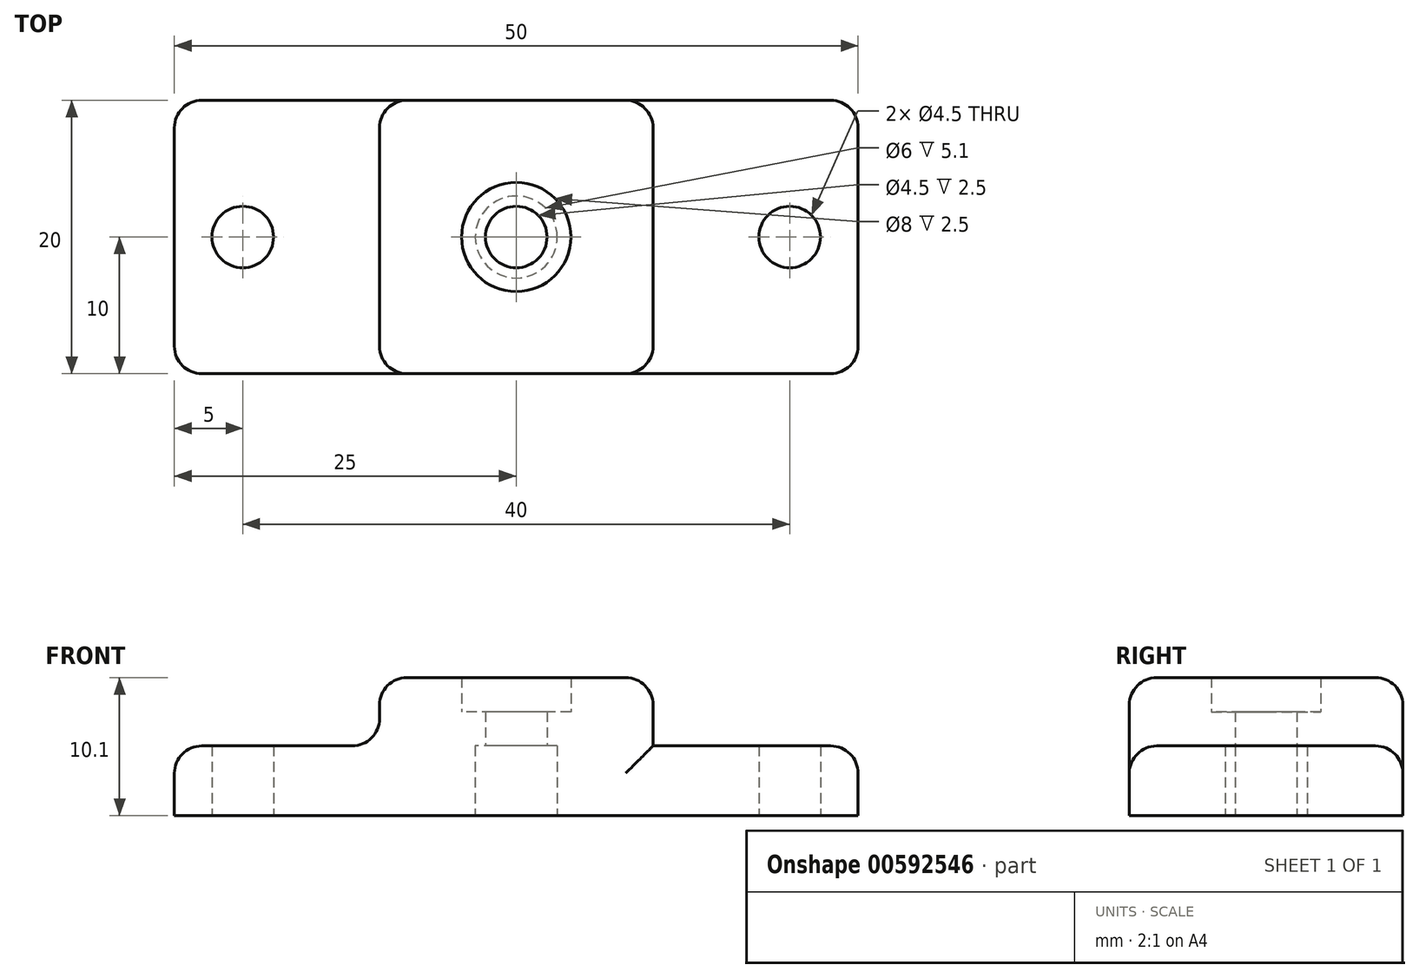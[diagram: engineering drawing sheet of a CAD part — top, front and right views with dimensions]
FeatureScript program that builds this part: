
annotation { "Feature Type Name" : "Feature", "Feature Type Description" : "" }
export const myFeature = defineFeature(function(context is Context, id is Id, definition is map)
    precondition{}
    {
        {
            var Q0;
            Q0=qCreatedBy(makeId("Top.planeOp"),FACE);
            var sketch = newSketch(context, id + "F0", { "sketchPlane" : qUnion([Q0])});
            skLineSegment(sketch, "E0.bottom", {"start": v(-25, 10) * mm, "end": v(25, 10) * mm});
            skLineSegment(sketch, "E0.top", {"start": v(-25, -10) * mm, "end": v(25, -10) * mm});
            skLineSegment(sketch, "E0.left", {"start": v(-25, 10) * mm, "end": v(-25, -10) * mm});
            skLineSegment(sketch, "E0.right", {"start": v(25, 10) * mm, "end": v(25, -10) * mm});
            skPoint(sketch, "E0.middle", {"position": v(0, 0) * mm});
            skCircle(sketch, "E1", {"center": v(0, 0) * mm, "radius": 3 * mm});
            skCircle(sketch, "E2", {"center": v(0, 0) * mm, "radius": 2.25 * mm});
            skCircle(sketch, "E3", {"center": v(0, 0) * mm, "radius": 4 * mm});
            skCircle(sketch, "E4", {"center": v(-20, 0) * mm, "radius": 2.25 * mm});
            skCircle(sketch, "E5", {"center": v(20, 0) * mm, "radius": 2.25 * mm});
            skSolve(sketch);
        }
        {
            var Q0;
            Q0=makeQuery(id+"F0.imprint","IMPRINT",FACE,{"disambiguationData":[TD([[makeQuery(id+"F0.imprint","IMPRINT",EDGE,{"derivedFrom":sQuery(id+"F0.wireOp",EDGE,"E0.bottom")}),-1.0]])]});
            var Q1;
            Q1=makeQuery(id+"F0.imprint","IMPRINT",FACE,{"disambiguationData":[TD([[makeQuery(id+"F0.imprint","IMPRINT",EDGE,{"derivedFrom":sQuery(id+"F0.wireOp",EDGE,"E1")}),-1.0]])]});
            extrude(context, id + "F1", {"entities" : qUnion([Q0, Q1]), "depth" : 5.1 * mm, "offsetDistance" : 25 * mm});
        }
        {
            var Q0;
            Q0=makeQuery(id+"F1.opExtrude","CAP_FACE",FACE,{"disambiguationData":[OSD([sQuery(id+"F0.wireOp",EDGE,"E0.bottom"),sQuery(id+"F0.wireOp",EDGE,"E0.top"),sQuery(id+"F0.wireOp",EDGE,"E0.left"),sQuery(id+"F0.wireOp",EDGE,"E0.right"),sQuery(id+"F0.wireOp",EDGE,"E1"),sQuery(id+"F0.wireOp",EDGE,"E4"),sQuery(id+"F0.wireOp",EDGE,"E5")])],"isStart":false});
            var sketch = newSketch(context, id + "F2", { "sketchPlane" : qUnion([Q0])});
            skLineSegment(sketch, "E6.bottom", {"start": v(10, -10) * mm, "end": v(-10, -10) * mm});
            skLineSegment(sketch, "E6.top", {"start": v(10, 10) * mm, "end": v(-10, 10) * mm});
            skLineSegment(sketch, "E6.left", {"start": v(10, -10) * mm, "end": v(10, 10) * mm});
            skLineSegment(sketch, "E6.right", {"start": v(-10, -10) * mm, "end": v(-10, 10) * mm});
            skPoint(sketch, "E6.middle", {"position": v(0, 0) * mm});
            skCircle(sketch, "E7.0", {"center": v(0, 0) * mm, "radius": 2.25 * mm});
            skSolve(sketch);
        }
        {
            var Q0;
            Q0=makeQuery(id+"F2.imprint","IMPRINT",FACE,{"disambiguationData":[TD([[makeQuery(id+"F2.imprint","IMPRINT",EDGE,{"derivedFrom":sQuery(id+"F2.wireOp",EDGE,"E6.bottom")}),1.0]])]});
            var Q1;
            Q1=makeQuery(id+"F2.imprint","IMPRINT",FACE,{"disambiguationData":[TD([[makeQuery(id+"F2.imprint","IMPRINT",EDGE,{"derivedFrom":sQuery(id+"F2.wireOp",EDGE,"E7.0")}),-1.0]])]});
            extrude(context, id + "F3", {"entities" : qUnion([Q0, Q1]), "operationType" : NewBodyOperationType.ADD, "depth" : 2.5 * mm, "offsetDistance" : 25 * mm});
        }
        {
            var Q0;
            Q0=makeQuery(id+"F3.opExtrude","CAP_FACE",FACE,{"disambiguationData":[OSD([sQuery(id+"F2.wireOp",EDGE,"E6.bottom"),sQuery(id+"F2.wireOp",EDGE,"E6.top"),sQuery(id+"F2.wireOp",EDGE,"E6.left"),sQuery(id+"F2.wireOp",EDGE,"E6.right"),sQuery(id+"F2.wireOp",EDGE,"E7.0")])],"isStart":false});
            var sketch = newSketch(context, id + "F4", { "sketchPlane" : qUnion([Q0])});
            skCircle(sketch, "E8.0", {"center": v(0, 0) * mm, "radius": 4 * mm});
            skSolve(sketch);
        }
        {
            var Q0;
            Q0=makeQuery(id+"F4.imprint","IMPRINT",FACE,{"disambiguationData":[TD([[makeQuery(id+"F4.imprint","IMPRINT",EDGE,{"derivedFrom":sQuery(id+"F4.wireOp",EDGE,"E8.0")}),-1.0]])]});
            extrude(context, id + "F5", {"entities" : qUnion([Q0]), "operationType" : NewBodyOperationType.ADD, "depth" : 2.5 * mm, "offsetDistance" : 25 * mm});
        }
        {
            var Q0;
            Q0=makeQuery(id+"F1.opExtrude","SWEPT_EDGE",EDGE,{"disambiguationData":[OSD([sQuery(id+"F0.wireOp",EDGE,"E0.top"),sQuery(id+"F0.wireOp",EDGE,"E0.left")])]});
            var Q1;
            Q1=makeQuery(id+"F1.opExtrude","SWEPT_EDGE",EDGE,{"disambiguationData":[OSD([sQuery(id+"F0.wireOp",EDGE,"E0.top"),sQuery(id+"F0.wireOp",EDGE,"E0.right")])]});
            var Q2;
            Q2=makeQuery(id+"F1.opExtrude","SWEPT_EDGE",EDGE,{"disambiguationData":[OSD([sQuery(id+"F0.wireOp",EDGE,"E0.bottom"),sQuery(id+"F0.wireOp",EDGE,"E0.right")])]});
            var Q3;
            Q3=makeQuery(id+"F1.opExtrude","CAP_EDGE",EDGE,{"disambiguationData":[OSD([sQuery(id+"F0.wireOp",EDGE,"E0.right")])],"isStart":false});
            var Q4;
            {var subQ0=sQuery(id+"F0.wireOp",EDGE,"E0.right");var subQ1=sQuery(id+"F0.wireOp",EDGE,"E0.top");Q4=makeQuery(id+"F3.boolean.opBoolean","SPLIT",EDGE,{"disambiguationData":[TD([makeQuery(id+"F1.opExtrude","SWEPT_FACE",FACE,{"disambiguationData":[OSD([subQ0])]})])],"derivedFrom":makeQuery(id+"F1.opExtrude","CAP_EDGE",EDGE,{"disambiguationData":[OSD([subQ1])],"isStart":false})});}
            var Q5;
            {var subQ0=sQuery(id+"F0.wireOp",EDGE,"E0.right");var subQ1=sQuery(id+"F0.wireOp",EDGE,"E0.bottom");Q5=makeQuery(id+"F3.boolean.opBoolean","SPLIT",EDGE,{"disambiguationData":[TD([makeQuery(id+"F1.opExtrude","SWEPT_FACE",FACE,{"disambiguationData":[OSD([subQ0])]})])],"derivedFrom":makeQuery(id+"F1.opExtrude","CAP_EDGE",EDGE,{"disambiguationData":[OSD([subQ1])],"isStart":false})});}
            var Q6;
            {var subQ0=sQuery(id+"F0.wireOp",EDGE,"E0.left");var subQ1=sQuery(id+"F0.wireOp",EDGE,"E0.top");Q6=makeQuery(id+"F3.boolean.opBoolean","SPLIT",EDGE,{"disambiguationData":[TD([makeQuery(id+"F1.opExtrude","SWEPT_FACE",FACE,{"disambiguationData":[OSD([subQ0])]})])],"derivedFrom":makeQuery(id+"F1.opExtrude","CAP_EDGE",EDGE,{"disambiguationData":[OSD([subQ1])],"isStart":false})});}
            var Q7;
            Q7=makeQuery(id+"F1.opExtrude","CAP_EDGE",EDGE,{"disambiguationData":[OSD([sQuery(id+"F0.wireOp",EDGE,"E0.left")])],"isStart":false});
            var Q8;
            {var subQ0=sQuery(id+"F0.wireOp",EDGE,"E0.left");var subQ1=sQuery(id+"F0.wireOp",EDGE,"E0.bottom");Q8=makeQuery(id+"F3.boolean.opBoolean","SPLIT",EDGE,{"disambiguationData":[TD([makeQuery(id+"F1.opExtrude","SWEPT_FACE",FACE,{"disambiguationData":[OSD([subQ0])]})])],"derivedFrom":makeQuery(id+"F1.opExtrude","CAP_EDGE",EDGE,{"disambiguationData":[OSD([subQ1])],"isStart":false})});}
            var Q9;
            Q9=makeQuery(id+"F1.opExtrude","SWEPT_EDGE",EDGE,{"disambiguationData":[OSD([sQuery(id+"F0.wireOp",EDGE,"E0.bottom"),sQuery(id+"F0.wireOp",EDGE,"E0.left")])]});
            var Q10;
            {var subQ0=sQuery(id+"Fktommp5rpzYMpY_1.wireOp",EDGE,"151076d3-d12a-400f-b86c-be84b4d02cd2.3");var subQ1=sQuery(id+"Fktommp5rpzYMpY_1.wireOp",EDGE,"151076d3-d12a-400f-b86c-be84b4d02cd2.1");Q10=makeQuery(id+"F5.boolean.opBoolean","MERGE",EDGE,{"derivedFrom":[makeQuery(id+"FSvqePnx5guRIMX_1.boolean.opBoolean","MERGE",EDGE,{"derivedFrom":[makeQuery(id+"F3.opExtrude","SWEPT_EDGE",EDGE,{"disambiguationData":[OSD([sQuery(id+"F0.wireOp",EDGE,"E0.top"),sQuery(id+"F2.wireOp",EDGE,"E6.bottom"),sQuery(id+"F2.wireOp",EDGE,"E6.left")])]}),makeQuery(id+"FSvqePnx5guRIMX_1.opExtrude","SWEPT_EDGE",EDGE,{"disambiguationData":[OSD([subQ1,subQ0])]})]}),makeQuery(id+"F5.opExtrude","SWEPT_EDGE",EDGE,{"disambiguationData":[OSD([subQ1,subQ0])]})]});}
            var Q11;
            {var subQ0=sQuery(id+"Fktommp5rpzYMpY_1.wireOp",EDGE,"151076d3-d12a-400f-b86c-be84b4d02cd2.2");var subQ1=sQuery(id+"Fktommp5rpzYMpY_1.wireOp",EDGE,"151076d3-d12a-400f-b86c-be84b4d02cd2.1");Q11=makeQuery(id+"F5.boolean.opBoolean","MERGE",EDGE,{"derivedFrom":[makeQuery(id+"FSvqePnx5guRIMX_1.boolean.opBoolean","MERGE",EDGE,{"derivedFrom":[makeQuery(id+"F3.opExtrude","SWEPT_EDGE",EDGE,{"disambiguationData":[OSD([sQuery(id+"F0.wireOp",EDGE,"E0.bottom"),sQuery(id+"F2.wireOp",EDGE,"E6.top"),sQuery(id+"F2.wireOp",EDGE,"E6.left")])]}),makeQuery(id+"FSvqePnx5guRIMX_1.opExtrude","SWEPT_EDGE",EDGE,{"disambiguationData":[OSD([subQ1,subQ0])]})]}),makeQuery(id+"F5.opExtrude","SWEPT_EDGE",EDGE,{"disambiguationData":[OSD([subQ1,subQ0])]})]});}
            var Q12;
            {var subQ0=sQuery(id+"Fktommp5rpzYMpY_1.wireOp",EDGE,"151076d3-d12a-400f-b86c-be84b4d02cd2.3");var subQ1=sQuery(id+"Fktommp5rpzYMpY_1.wireOp",EDGE,"151076d3-d12a-400f-b86c-be84b4d02cd2.0");Q12=makeQuery(id+"F5.boolean.opBoolean","MERGE",EDGE,{"derivedFrom":[makeQuery(id+"FSvqePnx5guRIMX_1.boolean.opBoolean","MERGE",EDGE,{"derivedFrom":[makeQuery(id+"F3.opExtrude","SWEPT_EDGE",EDGE,{"disambiguationData":[OSD([sQuery(id+"F0.wireOp",EDGE,"E0.top"),sQuery(id+"F2.wireOp",EDGE,"E6.bottom"),sQuery(id+"F2.wireOp",EDGE,"E6.right")])]}),makeQuery(id+"FSvqePnx5guRIMX_1.opExtrude","SWEPT_EDGE",EDGE,{"disambiguationData":[OSD([subQ1,subQ0])]})]}),makeQuery(id+"F5.opExtrude","SWEPT_EDGE",EDGE,{"disambiguationData":[OSD([subQ1,subQ0])]})]});}
            var Q13;
            {var subQ0=sQuery(id+"Fktommp5rpzYMpY_1.wireOp",EDGE,"151076d3-d12a-400f-b86c-be84b4d02cd2.2");var subQ1=sQuery(id+"Fktommp5rpzYMpY_1.wireOp",EDGE,"151076d3-d12a-400f-b86c-be84b4d02cd2.0");Q13=makeQuery(id+"F5.boolean.opBoolean","MERGE",EDGE,{"derivedFrom":[makeQuery(id+"FSvqePnx5guRIMX_1.boolean.opBoolean","MERGE",EDGE,{"derivedFrom":[makeQuery(id+"F3.opExtrude","SWEPT_EDGE",EDGE,{"disambiguationData":[OSD([sQuery(id+"F0.wireOp",EDGE,"E0.bottom"),sQuery(id+"F2.wireOp",EDGE,"E6.top"),sQuery(id+"F2.wireOp",EDGE,"E6.right")])]}),makeQuery(id+"FSvqePnx5guRIMX_1.opExtrude","SWEPT_EDGE",EDGE,{"disambiguationData":[OSD([subQ1,subQ0])]})]}),makeQuery(id+"F5.opExtrude","SWEPT_EDGE",EDGE,{"disambiguationData":[OSD([subQ1,subQ0])]})]});}
            var Q14;
            Q14=makeQuery(id+"F5.opExtrude","CAP_EDGE",EDGE,{"disambiguationData":[OSD([sQuery(id+"Fktommp5rpzYMpY_1.wireOp",EDGE,"151076d3-d12a-400f-b86c-be84b4d02cd2.1")])],"isStart":false});
            var Q15;
            Q15=makeQuery(id+"F5.opExtrude","CAP_EDGE",EDGE,{"disambiguationData":[OSD([sQuery(id+"Fktommp5rpzYMpY_1.wireOp",EDGE,"151076d3-d12a-400f-b86c-be84b4d02cd2.3")])],"isStart":false});
            var Q16;
            Q16=makeQuery(id+"F5.opExtrude","CAP_EDGE",EDGE,{"disambiguationData":[OSD([sQuery(id+"Fktommp5rpzYMpY_1.wireOp",EDGE,"151076d3-d12a-400f-b86c-be84b4d02cd2.0")])],"isStart":false});
            var Q17;
            Q17=makeQuery(id+"F5.opExtrude","CAP_EDGE",EDGE,{"disambiguationData":[OSD([sQuery(id+"Fktommp5rpzYMpY_1.wireOp",EDGE,"151076d3-d12a-400f-b86c-be84b4d02cd2.2")])],"isStart":false});
            var Q18;
            Q18=makeQuery(id+"F3.opExtrude","CAP_EDGE",EDGE,{"disambiguationData":[OSD([sQuery(id+"F2.wireOp",EDGE,"E6.left")])],"isStart":true});
            var Q19;
            Q19=makeQuery(id+"F3.opExtrude","CAP_EDGE",EDGE,{"disambiguationData":[OSD([sQuery(id+"F2.wireOp",EDGE,"E6.right")])],"isStart":true});
            var Q20;
            Q20=makeQuery(id+"F5.opExtrude","CAP_EDGE",EDGE,{"disambiguationData":[OSD([sQuery(id+"F2.wireOp",EDGE,"E6.bottom")])],"isStart":false});
            var Q21;
            Q21=makeQuery(id+"F5.opExtrude","CAP_EDGE",EDGE,{"disambiguationData":[OSD([sQuery(id+"F2.wireOp",EDGE,"E6.right")])],"isStart":false});
            var Q22;
            Q22=makeQuery(id+"F5.opExtrude","CAP_EDGE",EDGE,{"disambiguationData":[OSD([sQuery(id+"F2.wireOp",EDGE,"E6.top")])],"isStart":false});
            var Q23;
            Q23=makeQuery(id+"F5.opExtrude","CAP_EDGE",EDGE,{"disambiguationData":[OSD([sQuery(id+"F2.wireOp",EDGE,"E6.left")])],"isStart":false});
            fillet(context, id + "F6", {"entities" : qUnion([Q0, Q1, Q2, Q3, Q4, Q5, Q6, Q7, Q8, Q9, Q10, Q11, Q12, Q13, Q14, Q15, Q16, Q17, Q18, Q19, Q20, Q21, Q22, Q23]), "radius" : 2 * mm, "tangentPropagation" : true, "allowEdgeOverflow" : false});
        }
    });
